# Revit family: IS_Ceratherm200New_A5620_BIM_IT
name_source: partatom
category: Plumbing Fixtures
revit_build: Autodesk Revit MEP 2016 (Build: 20161004_0715(x64)
units: mm (PartAtom-declared; Revit-internal decimal feet)

## family parameters
Always vertical = No
Cut with Voids When Loaded = No
OmniClass Number = 23.45.55.17
OmniClass Title = Mixing Faucets
Part Type = Normal
Room Calculation Point = No
Round Connector Dimension = Use Diameter
Shared = No
Work Plane-Based = No

## types (1)
- A5620AA - CERATHERM 200 NEW V/D TH KIT2 EASY-B.
    Accessori = www.idealstandard.it
    AltezzaNominale = 157 mm  [stored 0.515092 ft]
    ApplicazioneMiscelatore = Monocomando
    Assembly Code = C1030200
    BIMobject category = Taps & Mixers
    BOSUseNativeGeometries = 1
    Brand url = http://www.idealstandard.co.uk
    Caratteristiche = Miscelatore termostatico ad incasso individuale con deviatore per vasca/doccia. Comando regolazione portata acqua (per entrambe le uscite). Lavora con corpo incasso EASY-BOX A1000NU, da ordinare separatamente. Il codice è comprensivo di parti esterne, cartuccia termostatica e deviatore.
    CodiceABarre = 4015413313339
    CodiceArticolo = A5620AA
    CodiceRiferimento = CERATHERM 200 NEW V/D TH KIT2 EASY-B.
    Colore = Cromato
    Connessione = Installazione
    CostoDiSostituzione = 0 $
    Description = CERATHERM 200 NEW V/D TH KIT2 EASY-B.
    Dimensione = 157 x 157 x 106
    DurataGaranzia = 5
    DurataGaranziaProdotti = 5
    EAN code = https://4015413313339
    Edition number = 1
    Finitura = Cromato
    FlussoDiPortata = 8 l/min @ 3bar
    Forma = Scultura
    Garanzia = Garanzia Idealstandard
    IFC Classification = Sanitary Terminal
    InformaziniGaranzia = www.idealstandard.it/garanzia.html
    InformazioniGaranzia = www.idealstandard.it/garanzia.html
    Installation instructions = http://www.idealstandard.it
    InstruzioniInstallazione = www.idealstandard.it/prodotti/html
    LarghezzaNominale = 157 mm  [stored 0.515092 ft]
    LunghezzaNominale = 106 mm
    Manufacturer name = Ideal Standard
    Material main = Brass
    Materiale = Ottone
    Model = A5620AA
    NBS Reference Code = 35-06-07
    NBS Reference Description = Bath Water Supply Fittings
    Nome = CERATHERM 200 NEW V/D TH KIT2 EASY-B.
    Nominal height = 157
    Nominal width = 157
    NumeroDiModello = A5620AA
    OmniClass Code = 23-31 11 00
    OmniClass Description = Faucets
    PartiDiRicambio = www.idealstandard.it/prodotti/html
    PesoNetto = 2,1 KG
    Pressione = 16 bar
    PressioneD'Esercizio = 1 to 5 bar
    Product Guid = 90f12d15-7124-4188-a8b2-1c74b08a0704
    Product SKU = A5620AA
    Product certification = http://www.idealstandard.it
    Product data url = https://bimobject.com
    Product family = CERATHERM 200 NEW
    Product group = Basin Mixer
    Product name = CERATHERM 200 NEW BATH & SHOWER THERMOSTATIC MIXER KIT2
    Product url = http://www.idealstandard.it
    QR code = http://bimobject.com
    Spazio = Interno
    Technical description = http://www.idealstandard.it
    Telefono = 800 652 290
    TipoDiDato = Fisso
    TipoMiscelatore = Miscelatore
    TipologiaDiMiscelatore = Miscelatore incasso vasca doccia elettronico
    URL = www.idealstandard.it
    Uniclass 1.4 Code = L8212
    Uniclass 1.4 Description = Fittings
    Uniclass 2.0 Code = PR-35-06-07
    Uniclass 2.0 Description = Bath Water Supply Fittings
    Uniclass 2015 Code = Pr_40_20_87_10
    Uniclass 2015 Name = Bath thermostatic water supply sets
    UnitaDurata = anni
    UnitaDurataGaranzia = anni
    UnitaLineare = milimetri
    UnitaVolume = Litri
    Versione = 1.0
    Weight Net (Kg) = 2.1

note: [stored X ft] marks values corroborated as IEEE doubles in the binary element streams (Revit-internal decimal feet)

## geometry (parser evidence)
native form markers: Blend x4, Sweep x1
no freeform markers — native parametric forms only
